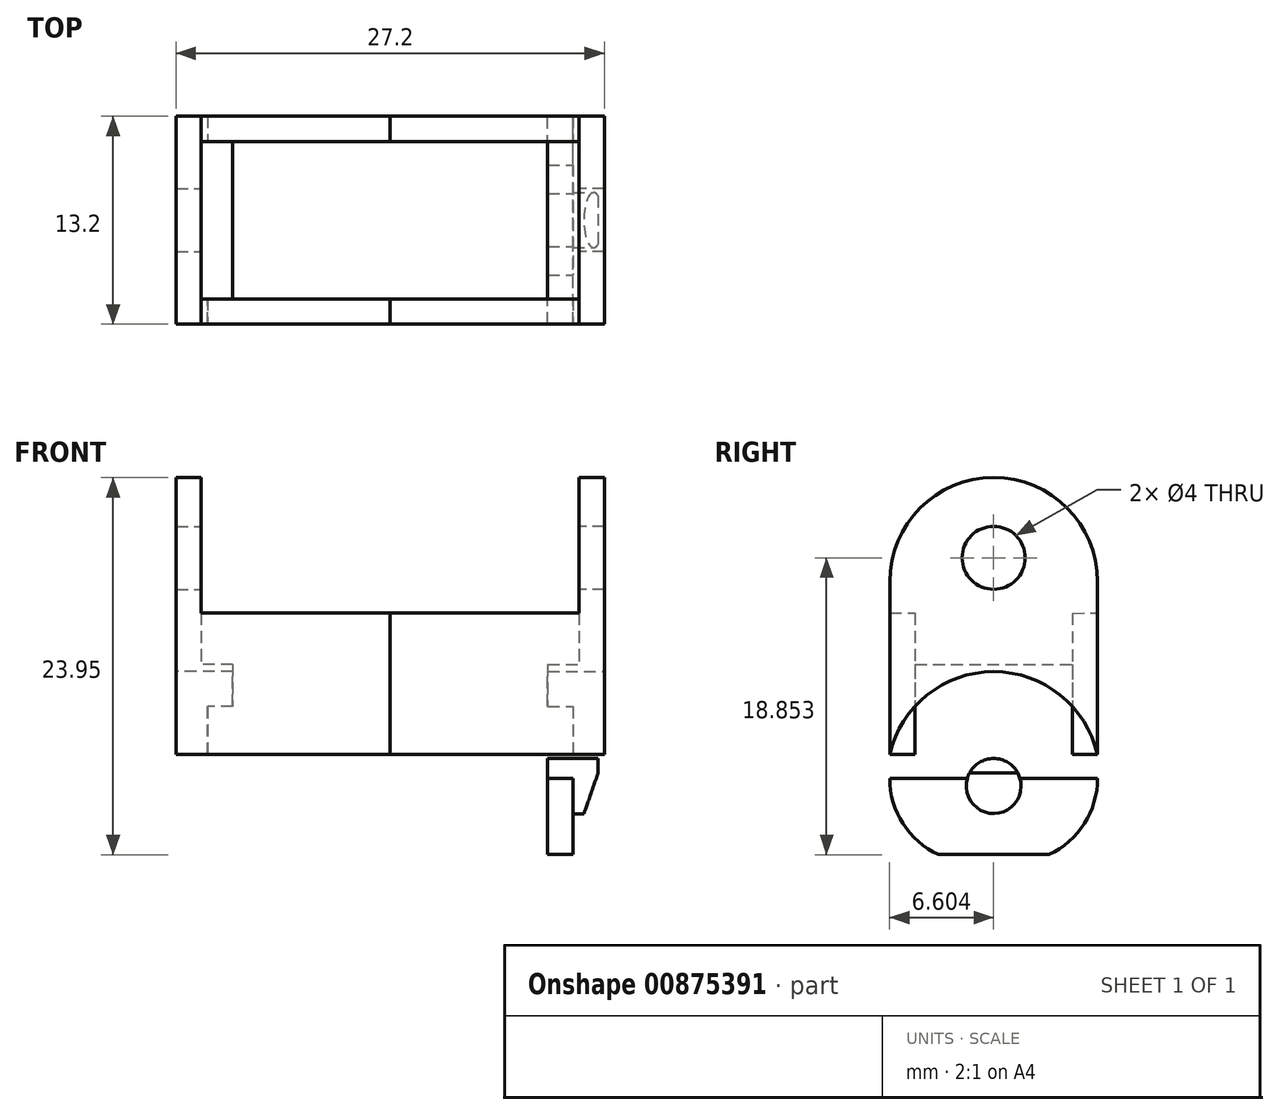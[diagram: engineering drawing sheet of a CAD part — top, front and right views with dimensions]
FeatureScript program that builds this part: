
annotation { "Feature Type Name" : "Feature", "Feature Type Description" : "" }
export const myFeature = defineFeature(function(context is Context, id is Id, definition is map)
    precondition{}
    {
        {
            var Q0;
            Q0=qCreatedBy(makeId("Right.planeOp"),FACE);
            cPlane(context, id + "F0", {"entities" : qUnion([Q0]), "cplaneType" : CPlaneType.OFFSET, "offset" : 11.6 * mm, "width" : 150 * mm, "height" : 150 * mm});
        }
        {
            var Q0;
            Q0=qCreatedBy(id+"F0.planeOp",FACE);
            var sketch = newSketch(context, id + "F1", { "sketchPlane" : qUnion([Q0])});
            skLineSegment(sketch, "E0.bottom", {"start": v(-1.77, -12.7) * mm, "end": v(11.43, -12.7) * mm});
            skLineSegment(sketch, "E0.top", {"start": v(-1.77, -25.2) * mm, "end": v(11.43, -25.2) * mm});
            skLineSegment(sketch, "E0.left", {"start": v(-1.77, -12.7) * mm, "end": v(-1.77, -25.2) * mm});
            skLineSegment(sketch, "E0.right", {"start": v(11.43, -12.7) * mm, "end": v(11.43, -25.2) * mm});
            skArc(sketch, "E1", {"start": v(11.43, -12.7) * mm, "mid": v(4.83, -6.1) * mm, "end": v(-1.77, -12.7) * mm});
            skLineSegment(sketch, "E2", {"start": v(8.33, -30.06) * mm, "end": v(1.33, -30.06) * mm});
            skCircle(sketch, "E3", {"center": v(4.83, -11.2) * mm, "radius": 2 * mm});
            skCircle(sketch, "E4", {"center": v(4.83, -25.7) * mm, "radius": 1.75 * mm});
            skPoint(sketch, "E5", {"position": v(4.83, -30.06) * mm});
            skLineSegment(sketch, "E6", {"start": v(-0.17, -17.98) * mm, "end": v(9.83, -17.98) * mm});
            skLineSegment(sketch, "E7.bottom", {"start": v(-1.77, -12.7) * mm, "end": v(-0.17, -12.7) * mm});
            skLineSegment(sketch, "E7.top", {"start": v(-1.77, -25.2) * mm, "end": v(-0.17, -25.2) * mm});
            skLineSegment(sketch, "E7.right", {"start": v(-0.17, -14.7) * mm, "end": v(-0.17, -23.7) * mm});
            skLineSegment(sketch, "E8.bottom", {"start": v(11.43, -12.7) * mm, "end": v(9.83, -12.7) * mm});
            skLineSegment(sketch, "E8.top", {"start": v(11.43, -25.2) * mm, "end": v(9.83, -25.2) * mm});
            skLineSegment(sketch, "E8.right", {"start": v(9.83, -14.73) * mm, "end": v(9.83, -23.7) * mm});
            skLineSegment(sketch, "E9", {"start": v(-1.77, -23.7) * mm, "end": v(-0.17, -23.7) * mm});
            skLineSegment(sketch, "E10", {"start": v(11.43, -23.7) * mm, "end": v(9.83, -23.7) * mm});
            skLineSegment(sketch, "E11", {"start": v(-1.77, -14.7) * mm, "end": v(-0.17, -14.7) * mm});
            skLineSegment(sketch, "E12", {"start": v(9.83, -14.73) * mm, "end": v(11.43, -14.7) * mm});
            skArc(sketch, "E13", {"start": v(11.43, -23.7) * mm, "mid": v(4.83, -18.44) * mm, "end": v(-1.77, -23.7) * mm});
            skArc(sketch, "E14", {"start": v(8.33, -30.06) * mm, "mid": v(10.6, -28.09) * mm, "end": v(11.43, -25.2) * mm});
            skArc(sketch, "E15", {"start": v(-1.77, -25.2) * mm, "mid": v(-0.92, -28.09) * mm, "end": v(1.33, -30.06) * mm});
            skSolve(sketch);
        }
        {
            var Q0;
            {var subQ0=sQuery(id+"FKfbHqh6FhteA2g_133.wireOp",EDGE,"3cAmnfbS-M9VH-9QOX-gIRw-Wr4FXjOXWDfN");Q0=makeQuery(id+"FKfbHqh6FhteA2g_133.imprint","IMPRINT",FACE,{"disambiguationData":[TD([[makeQuery(id+"FKfbHqh6FhteA2g_133.imprint","IMPRINT",EDGE,{"derivedFrom":subQ0}),1.0]])]});}
            var Q1;
            {var subQ0=sQuery(id+"FKfbHqh6FhteA2g_133.wireOp",EDGE,"3cAmnfbS-M9VH-9QOX-gIRw-Wr4FXjOXWDfN");Q1=makeQuery(id+"FKfbHqh6FhteA2g_133.imprint","IMPRINT",FACE,{"disambiguationData":[TD([[makeQuery(id+"FKfbHqh6FhteA2g_133.imprint","IMPRINT",EDGE,{"derivedFrom":subQ0}),-1.0]])]});}
            var Q2;
            {var subQ0=sQuery(id+"FKfbHqh6FhteA2g_133.wireOp",EDGE,"1o8B24JB-Kbt3-edzl-KQu9-GT3aDwbG8khO.right");var subQ6=sQuery(id+"FKfbHqh6FhteA2g_133.wireOp",EDGE,"3cAmnfbS-M9VH-9QOX-gIRw-Wr4FXjOXWDfN");var subQ7=makeQuery(id+"FKfbHqh6FhteA2g_133.imprint","INTERSECT",VERTEX,{"derivedFrom":[subQ6,subQ0]});Q2=makeQuery(id+"FKfbHqh6FhteA2g_133.imprint","IMPRINT",FACE,{"disambiguationData":[TD([[makeQuery(id+"FKfbHqh6FhteA2g_133.imprint","IMPRINT",EDGE,{"disambiguationData":[TD([[subQ7,-1.0]])],"derivedFrom":subQ6}),1.0]])]});}
            var Q3;
            {var subQ0=sQuery(id+"F1.wireOp",EDGE,"E6");Q3=makeQuery(id+"F1.imprint","IMPRINT",FACE,{"disambiguationData":[TD([[makeQuery(id+"F1.imprint","IMPRINT",EDGE,{"derivedFrom":subQ0}),-1.0]])]});}
            var Q4;
            {var subQ9=sQuery(id+"F1.wireOp",EDGE,"E7.top");Q4=makeQuery(id+"F1.imprint","IMPRINT",FACE,{"disambiguationData":[TD([[makeQuery(id+"F1.imprint","IMPRINT",EDGE,{"derivedFrom":subQ9}),1.0]])]});}
            var Q5;
            Q5=makeQuery(id+"F1.imprint","IMPRINT",FACE,{"disambiguationData":[TD([[makeQuery(id+"F1.imprint","IMPRINT",EDGE,{"derivedFrom":sQuery(id+"F1.wireOp",EDGE,"E2")}),-1.0]])]});
            var Q6;
            {var subQ0=sQuery(id+"F1.wireOp",EDGE,"E4");var subQ1=sQuery(id+"F1.wireOp",EDGE,"E0.top");var subQ2=makeQuery(id+"F1.imprint","INTERSECT",VERTEX,{"disambiguationData":[OD(0.0)],"derivedFrom":[subQ1,subQ0]});Q6=makeQuery(id+"F1.imprint","IMPRINT",FACE,{"disambiguationData":[TD([[makeQuery(id+"F1.imprint","IMPRINT",EDGE,{"disambiguationData":[TD([[subQ2,-1.0]])],"derivedFrom":subQ1}),-1.0]])]});}
            var Q7;
            {var subQ0=sQuery(id+"F1.wireOp",EDGE,"E4");var subQ1=sQuery(id+"F1.wireOp",EDGE,"E0.top");var subQ2=makeQuery(id+"F1.imprint","INTERSECT",VERTEX,{"disambiguationData":[OD(0.0)],"derivedFrom":[subQ1,subQ0]});Q7=makeQuery(id+"F1.imprint","IMPRINT",FACE,{"disambiguationData":[TD([[makeQuery(id+"F1.imprint","IMPRINT",EDGE,{"disambiguationData":[TD([[subQ2,-1.0]])],"derivedFrom":subQ1}),1.0]])]});}
            var Q8;
            {var subQ0=sQuery(id+"F1.wireOp",EDGE,"E10");Q8=makeQuery(id+"F1.imprint","IMPRINT",FACE,{"disambiguationData":[TD([[makeQuery(id+"F1.imprint","IMPRINT",EDGE,{"derivedFrom":subQ0}),-1.0]])]});}
            var Q9;
            {var subQ0=sQuery(id+"F1.wireOp",EDGE,"E9");Q9=makeQuery(id+"F1.imprint","IMPRINT",FACE,{"disambiguationData":[TD([[makeQuery(id+"F1.imprint","IMPRINT",EDGE,{"derivedFrom":subQ0}),1.0]])]});}
            extrude(context, id + "F2", {"entities" : qUnion([Q0, Q1, Q2, Q3, Q4, Q5, Q6, Q7, Q8, Q9]), "oppositeDirection" : true, "depth" : 1.6 * mm, "offsetDistance" : 25 * mm});
        }
        {
            var Q0;
            {var subQ6=sQuery(id+"F1.wireOp",EDGE,"E6");Q0=makeQuery(id+"F1.imprint","IMPRINT",FACE,{"disambiguationData":[TD([[makeQuery(id+"F1.imprint","IMPRINT",EDGE,{"derivedFrom":subQ6}),1.0]])]});}
            var Q1;
            Q1=makeQuery(id+"F1.imprint","IMPRINT",FACE,{"disambiguationData":[TD([[makeQuery(id+"F1.imprint","IMPRINT",EDGE,{"derivedFrom":sQuery(id+"F1.wireOp",EDGE,"E1")}),1.0]])]});
            var Q2;
            {var subQ0=sQuery(id+"F1.wireOp",EDGE,"E6");Q2=makeQuery(id+"F1.imprint","IMPRINT",FACE,{"disambiguationData":[TD([[makeQuery(id+"F1.imprint","IMPRINT",EDGE,{"derivedFrom":subQ0}),-1.0]])]});}
            extrude(context, id + "F3", {"entities" : qUnion([Q0, Q1, Q2]), "operationType" : NewBodyOperationType.ADD, "depth" : 2 * mm, "offsetDistance" : 25 * mm});
        }
        {
            var Q0;
            {var subQ6=sQuery(id+"F1.wireOp",EDGE,"E6");Q0=makeQuery(id+"F1.imprint","IMPRINT",FACE,{"disambiguationData":[TD([[makeQuery(id+"F1.imprint","IMPRINT",EDGE,{"derivedFrom":subQ6}),1.0]])]});}
            var Q1;
            Q1=makeQuery(id+"F1.imprint","IMPRINT",FACE,{"disambiguationData":[TD([[makeQuery(id+"F1.imprint","IMPRINT",EDGE,{"derivedFrom":sQuery(id+"F1.wireOp",EDGE,"E1")}),1.0]])]});
            extrude(context, id + "F4", {"entities" : qUnion([Q0, Q1]), "operationType" : NewBodyOperationType.REMOVE, "depth" : 0.4 * mm, "offsetDistance" : 25 * mm});
        }
        {
            var Q0;
            {var subQ0=sQuery(id+"F1.wireOp",EDGE,"E12");Q0=makeQuery(id+"F1.imprint","IMPRINT",FACE,{"disambiguationData":[TD([[makeQuery(id+"F1.imprint","IMPRINT",EDGE,{"derivedFrom":subQ0}),-1.0]])]});}
            var Q1;
            {var subQ4=sQuery(id+"F1.wireOp",EDGE,"E11");Q1=makeQuery(id+"F1.imprint","IMPRINT",FACE,{"disambiguationData":[TD([[makeQuery(id+"F1.imprint","IMPRINT",EDGE,{"derivedFrom":subQ4}),-1.0]])]});}
            var Q2;
            {var subQ0=sQuery(id+"F1.wireOp",EDGE,"E10");Q2=makeQuery(id+"F1.imprint","IMPRINT",FACE,{"disambiguationData":[TD([[makeQuery(id+"F1.imprint","IMPRINT",EDGE,{"derivedFrom":subQ0}),-1.0]])]});}
            var Q3;
            {var subQ0=sQuery(id+"F1.wireOp",EDGE,"E9");Q3=makeQuery(id+"F1.imprint","IMPRINT",FACE,{"disambiguationData":[TD([[makeQuery(id+"F1.imprint","IMPRINT",EDGE,{"derivedFrom":subQ0}),1.0]])]});}
            extrude(context, id + "F5", {"entities" : qUnion([Q0, Q1, Q2, Q3]), "oppositeDirection" : true, "depth" : 11.6 * mm, "offsetDistance" : 25 * mm});
        }
        {
            var Q0;
            {var subQ4=sQuery(id+"F1.wireOp",EDGE,"E11");Q0=makeQuery(id+"F1.imprint","IMPRINT",FACE,{"disambiguationData":[TD([[makeQuery(id+"F1.imprint","IMPRINT",EDGE,{"derivedFrom":subQ4}),-1.0]])]});}
            var Q1;
            {var subQ0=sQuery(id+"F1.wireOp",EDGE,"E12");Q1=makeQuery(id+"F1.imprint","IMPRINT",FACE,{"disambiguationData":[TD([[makeQuery(id+"F1.imprint","IMPRINT",EDGE,{"derivedFrom":subQ0}),-1.0]])]});}
            extrude(context, id + "F6", {"entities" : qUnion([Q0, Q1]), "operationType" : NewBodyOperationType.ADD, "depth" : 2 * mm, "offsetDistance" : 25 * mm});
        }
        {
            var Q0;
            {var subQ0=sQuery(id+"F1.wireOp",EDGE,"E4");var subQ1=sQuery(id+"F1.wireOp",EDGE,"E0.top");var subQ2=makeQuery(id+"F1.imprint","INTERSECT",VERTEX,{"disambiguationData":[OD(0.0)],"derivedFrom":[subQ1,subQ0]});Q0=makeQuery(id+"F1.imprint","IMPRINT",FACE,{"disambiguationData":[TD([[makeQuery(id+"F1.imprint","IMPRINT",EDGE,{"disambiguationData":[TD([[subQ2,-1.0]])],"derivedFrom":subQ1}),1.0]])]});}
            var Q1;
            {var subQ0=sQuery(id+"F1.wireOp",EDGE,"E4");var subQ1=sQuery(id+"F1.wireOp",EDGE,"E0.top");var subQ2=makeQuery(id+"F1.imprint","INTERSECT",VERTEX,{"disambiguationData":[OD(0.0)],"derivedFrom":[subQ1,subQ0]});Q1=makeQuery(id+"F1.imprint","IMPRINT",FACE,{"disambiguationData":[TD([[makeQuery(id+"F1.imprint","IMPRINT",EDGE,{"disambiguationData":[TD([[subQ2,-1.0]])],"derivedFrom":subQ1}),-1.0]])]});}
            extrude(context, id + "F7", {"entities" : qUnion([Q0, Q1]), "operationType" : NewBodyOperationType.ADD, "depth" : 1.6 * mm, "offsetDistance" : 25 * mm});
        }
        {
            var Q0;
            Q0=qCreatedBy(makeId("Front.planeOp"),FACE);
            var sketch = newSketch(context, id + "F8", { "sketchPlane" : qUnion([Q0])});
            skLineSegment(sketch, "E16.bottom", {"start": v(13.3, -24.59) * mm, "end": v(14.51, -25) * mm});
            skLineSegment(sketch, "E16.top", {"start": v(12.27, -27.54) * mm, "end": v(13.48, -27.96) * mm});
            skLineSegment(sketch, "E16.left", {"start": v(13.3, -24.59) * mm, "end": v(12.27, -27.54) * mm});
            skLineSegment(sketch, "E16.right", {"start": v(14.51, -25) * mm, "end": v(13.48, -27.96) * mm});
            skSolve(sketch);
        }
        {
            var Q0;
            Q0=qSketchRegion(id+"F8",true);
            extrude(context, id + "F9", {"entities" : qUnion([Q0]), "operationType" : NewBodyOperationType.REMOVE, "oppositeDirection" : true, "depth" : 25 * mm, "offsetDistance" : 25 * mm});
        }
        {
            var Q0;
            Q0=makeQuery(id+"F2.opExtrude","SWEPT_BODY",BODY,{"disambiguationData":[OSD([sQuery(id+"F1.wireOp",EDGE,"E2"),sQuery(id+"F1.wireOp",EDGE,"3374eb2c-ece4-431a-ab59-06c23a874628"),sQuery(id+"F1.wireOp",EDGE,"536c7ca2-0d11-40ae-a7ce-e5075c13715a"),sQuery(id+"F1.wireOp",EDGE,"E6"),sQuery(id+"F1.wireOp",EDGE,"E0.left"),sQuery(id+"F1.wireOp",EDGE,"E7.right"),sQuery(id+"F1.wireOp",EDGE,"E0.right"),sQuery(id+"F1.wireOp",EDGE,"E8.right"),sQuery(id+"F1.wireOp",EDGE,"E13")])]});
            var Q1;
            Q1=qCreatedBy(makeId("Right.planeOp"),FACE);
            mirror(context, id + "F10", {"operationType" : NewBodyOperationType.ADD, "entities" : qUnion([Q0]), "mirrorPlane" : qUnion([Q1])});
        }
        {
            var Q0;
            Q0=makeQuery(id+"F2.opExtrude","SWEPT_BODY",BODY,{"disambiguationData":[OSD([sQuery(id+"F1.wireOp",EDGE,"E2"),sQuery(id+"F1.wireOp",EDGE,"E6"),sQuery(id+"F1.wireOp",EDGE,"E0.left"),sQuery(id+"F1.wireOp",EDGE,"E7.right"),sQuery(id+"F1.wireOp",EDGE,"E0.right"),sQuery(id+"F1.wireOp",EDGE,"E8.right"),sQuery(id+"F1.wireOp",EDGE,"E13"),sQuery(id+"F1.wireOp",EDGE,"E14"),sQuery(id+"F1.wireOp",EDGE,"E15")])]});
            transform(context, id + "F11", {"entities" : qUnion([Q0]), "transformType" : TransformType.TRANSLATION_3D, "dx" : 0 * mm, "dy" : 0 * mm, "dz" : 0 * mm, "makeCopy" : true});
        }
        {
            var Q0;
            Q0=makeQuery(id+"F11.opPattern","COPY",BODY,{"derivedFrom":makeQuery(id+"F2.opExtrude","SWEPT_BODY",BODY,{"disambiguationData":[OSD([sQuery(id+"F1.wireOp",EDGE,"E2"),sQuery(id+"F1.wireOp",EDGE,"E6"),sQuery(id+"F1.wireOp",EDGE,"E0.left"),sQuery(id+"F1.wireOp",EDGE,"E7.right"),sQuery(id+"F1.wireOp",EDGE,"E0.right"),sQuery(id+"F1.wireOp",EDGE,"E8.right"),sQuery(id+"F1.wireOp",EDGE,"E13"),sQuery(id+"F1.wireOp",EDGE,"E14"),sQuery(id+"F1.wireOp",EDGE,"E15")])]}),"instanceName":"1"});
            deleteBodies(context, id + "F12", {"entities" : qUnion([Q0])});
        }
    });
